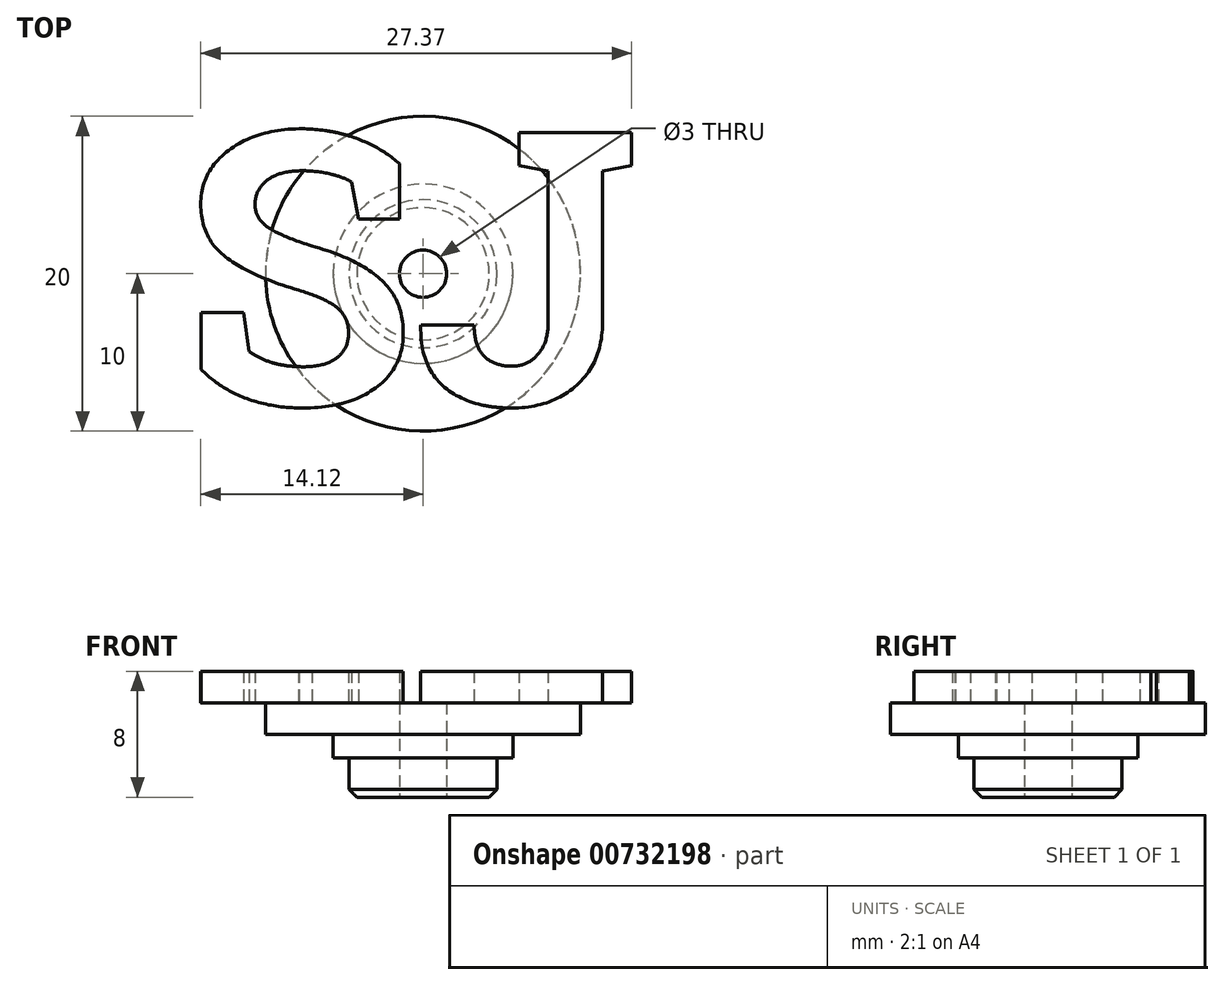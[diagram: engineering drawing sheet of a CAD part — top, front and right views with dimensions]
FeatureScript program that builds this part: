
annotation { "Feature Type Name" : "Feature", "Feature Type Description" : "" }
export const myFeature = defineFeature(function(context is Context, id is Id, definition is map)
    precondition{}
    {
        {
            var Q0;
            Q0=qCreatedBy(makeId("Top.planeOp"),FACE);
            var sketch = newSketch(context, id + "F0", { "sketchPlane" : qUnion([Q0])});
            skCircle(sketch, "E0", {"center": v(0, 0) * mm, "radius": 10 * mm});
            skLineSegment(sketch, "E1", {"start": v(0, 25.77) * mm, "end": v(0, -30.08) * mm, "construction": true});
            skLineSegment(sketch, "E2", {"start": v(23.36, 0) * mm, "end": v(-28.07, 0) * mm, "construction": true});
            skSolve(sketch);
        }
        {
            var Q0;
            Q0=qSketchRegion(id+"F0",true);
            extrude(context, id + "F1", {"entities" : qUnion([Q0]), "depth" : 2 * mm, "offsetDistance" : 25 * mm});
        }
        {
            var Q0;
            Q0=makeQuery(id+"F1.opExtrude","CAP_FACE",FACE,{"disambiguationData":[OSD([sQuery(id+"F0.wireOp",EDGE,"E0")])],"isStart":true});
            var sketch = newSketch(context, id + "F2", { "sketchPlane" : qUnion([Q0])});
            skCircle(sketch, "E3", {"center": v(0, 0) * mm, "radius": 4.7 * mm});
            skSolve(sketch);
        }
        {
            var Q0;
            Q0=qSketchRegion(id+"F2",true);
            extrude(context, id + "F3", {"entities" : qUnion([Q0]), "operationType" : NewBodyOperationType.ADD, "depth" : 4 * mm, "offsetDistance" : 25 * mm});
        }
        {
            var Q0;
            Q0=makeQuery(id+"F3.opExtrude","CAP_EDGE",EDGE,{"disambiguationData":[OSD([sQuery(id+"F2.wireOp",EDGE,"E3")])],"isStart":false});
            chamfer(context, id + "F4", {"entities" : qUnion([Q0]), "width" : .5 * mm, "tangentPropagation" : true});
        }
        {
            var Q0;
            Q0=makeQuery(id+"F3.opExtrude","CAP_FACE",FACE,{"disambiguationData":[OSD([sQuery(id+"F2.wireOp",EDGE,"E3")])],"isStart":false});
            var sketch = newSketch(context, id + "F5", { "sketchPlane" : qUnion([Q0])});
            skCircle(sketch, "E4", {"center": v(0, 0) * mm, "radius": 1.5 * mm});
            skSolve(sketch);
        }
        {
            var Q0;
            Q0=qSketchRegion(id+"F5",true);
            extrude(context, id + "F6", {"entities" : qUnion([Q0]), "operationType" : NewBodyOperationType.REMOVE, "oppositeDirection" : true, "depth" : 25 * mm, "offsetDistance" : 25 * mm});
        }
        {
            var Q0;
            Q0=makeQuery(id+"F1.opExtrude","CAP_FACE",FACE,{"disambiguationData":[OSD([sQuery(id+"F0.wireOp",EDGE,"E0")])],"isStart":true});
            var sketch = newSketch(context, id + "F7", { "sketchPlane" : qUnion([Q0])});
            skCircle(sketch, "E5.0", {"center": v(0, 0) * mm, "radius": 5.7 * mm});
            skCircle(sketch, "E6.0", {"center": v(0, 0) * mm, "radius": 4.7 * mm});
            skSolve(sketch);
        }
        {
            var Q0;
            Q0=qSketchRegion(id+"F7",true);
            extrude(context, id + "F8", {"entities" : qUnion([Q0]), "operationType" : NewBodyOperationType.ADD, "depth" : 1.5 * mm, "offsetDistance" : 25 * mm});
        }
        {
            var Q0;
            Q0=makeQuery(id+"F1.opExtrude","CAP_FACE",FACE,{"disambiguationData":[OSD([sQuery(id+"F0.wireOp",EDGE,"E0")])],"isStart":false});
            var sketch = newSketch(context, id + "F9", { "sketchPlane" : qUnion([Q0])});
            skText(sketch, "E7", { "text": "SJ", "fontName": "RobotoSlab-Bold.ttf"});
            const initialGuessF9  = {"E7": [-0.01527, -0.00828, 1, 0, 0.01747]};
            skSetInitialGuess(sketch, initialGuessF9);
            skSolve(sketch);
        }
        {
            var Q0;
            Q0 = qSketchRegion(id + "F9", true);
            extrude(context, id + "F10", {"entities" : qUnion([Q0]), "operationType" : NewBodyOperationType.ADD, "depth" : 2 * mm, "offsetDistance" : 25 * mm});
        }
    });
